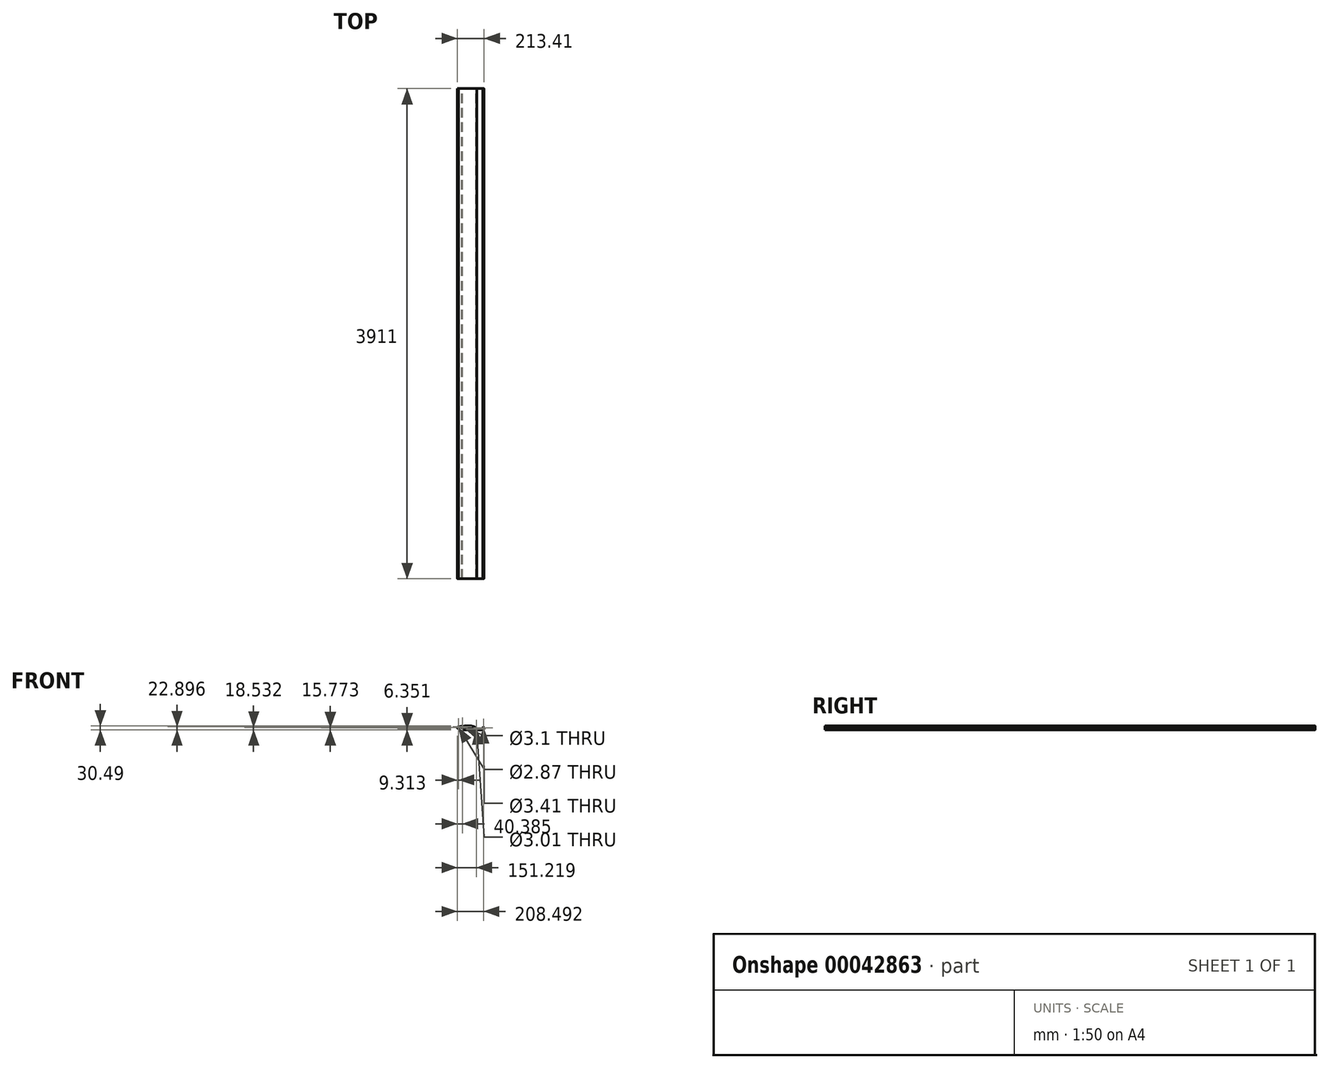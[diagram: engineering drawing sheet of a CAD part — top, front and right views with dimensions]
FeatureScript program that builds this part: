
annotation { "Feature Type Name" : "Feature", "Feature Type Description" : "" }
export const myFeature = defineFeature(function(context is Context, id is Id, definition is map)
    precondition{}
    {
        {
            var Q0;
            Q0=qCreatedBy(makeId("Front.planeOp"),FACE);
            var sketch = newSketch(context, id + "F0", { "sketchPlane" : qUnion([Q0])});
            skCircle(sketch, "E0", {"center": v(-106.3, 13.54) * mm, "radius": 1.44 * mm});
            skCircle(sketch, "E1", {"center": v(-75.23, 17.9) * mm, "radius": 1.55 * mm});
            skCircle(sketch, "E2", {"center": v(35.6, 1.36) * mm, "radius": 1.5 * mm});
            skCircle(sketch, "E3", {"center": v(92.88, 10.78) * mm, "radius": 1.7 * mm});
            skFitSpline(sketch, "E4", {"points": [v(-107.48, 19.59) * mm, v(-60.2, 23.95) * mm, v(-6.86, 24.97) * mm, v(22.27, 16.71) * mm, v(39.36, 3.6) * mm], "startDerivative": vector(161.35, 14.36) * mm, "endDerivative": vector(26.37, -21.19) * mm});
            skLineSegment(sketch, "E5", {"start": v(40.27, -1.32) * mm, "end": v(87.46, -1.24) * mm});
            skFitSpline(sketch, "E6", {"points": [v(40.3, -3.85) * mm, v(90, 0.2) * mm, v(93, 9.4) * mm], "startDerivative": vector(8.74, 2.96) * mm, "endDerivative": vector(0.7, 5.97) * mm});
            skLineSegment(sketch, "E7", {"start": v(92.97, 5.13) * mm, "end": v(86.47, 9.2) * mm});
            skLineSegment(sketch, "E8", {"start": v(86.47, 9.2) * mm, "end": v(91.56, 17) * mm});
            skLineSegment(sketch, "E9", {"start": v(96.31, 14.3) * mm, "end": v(91.56, 17) * mm});
            skLineSegment(sketch, "E10", {"start": v(-68.16, -4.99) * mm, "end": v(-80.63, 17.44) * mm});
            skLineSegment(sketch, "E11", {"start": v(-116.11, 7.62) * mm, "end": v(-113.4, 14.94) * mm});
            skLineSegment(sketch, "E12", {"start": v(-116.11, 7.62) * mm, "end": v(-111.23, 5.8) * mm});
            skLineSegment(sketch, "E13", {"start": v(-111.23, 5.8) * mm, "end": v(-109.3, 11.02) * mm});
            skArc(sketch, "E14", {"start": v(97.6, 9.4) * mm, "mid": v(97.64, 12.03) * mm, "end": v(96.31, 14.3) * mm});
            skArc(sketch, "E15", {"start": v(40.27, -1.32) * mm, "mid": v(40.61, 1.3) * mm, "end": v(39.35, 3.6) * mm});
            skArc(sketch, "E16", {"start": v(-107.48, 19.59) * mm, "mid": v(-111.19, 18.22) * mm, "end": v(-113.4, 14.94) * mm});
            skArc(sketch, "E17", {"start": v(-109.3, 11.02) * mm, "mid": v(-103.78, 10.54) * mm, "end": v(-103.3, 16.06) * mm});
            skLineSegment(sketch, "E18", {"start": v(-103.3, 16.06) * mm, "end": v(-80.63, 17.44) * mm});
            skLineSegment(sketch, "E19", {"start": v(-68.16, -4.99) * mm, "end": v(91.56, -4.99) * mm});
            skLineSegment(sketch, "E20", {"start": v(97.6, 9.4) * mm, "end": v(91.56, -4.99) * mm});
            skLineSegment(sketch, "E21", {"start": v(-72.14, 20.7) * mm, "end": v(-72.14, 13.78) * mm});
            skLineSegment(sketch, "E22", {"start": v(-72.14, 13.78) * mm, "end": v(-75.93, 13.78) * mm});
            skLineSegment(sketch, "E23", {"start": v(-75.93, 13.78) * mm, "end": v(-66.55, -2.48) * mm});
            skLineSegment(sketch, "E24", {"start": v(-66.55, -2.48) * mm, "end": v(31.06, -2.48) * mm});
            skLineSegment(sketch, "E25", {"start": v(31.06, -2.48) * mm, "end": v(31.06, 1.08) * mm});
            skLineSegment(sketch, "E26", {"start": v(31.06, 1.08) * mm, "end": v(33.93, 5.24) * mm});
            skFitSpline(sketch, "E27", {"points": [v(-107.28, 17.33) * mm, v(-103.91, 17.63) * mm, v(-97.2, 18.27) * mm, v(-87.04, 19.28) * mm, v(-78.4, 20.12) * mm, v(-71.32, 20.77) * mm, v(-65.91, 21.23) * mm, v(-60.39, 21.67) * mm, v(-54.72, 22.07) * mm, v(-48.96, 22.43) * mm, v(-41.23, 22.84) * mm, v(-33.5, 23.12) * mm, v(-25.98, 23.24) * mm, v(-20.49, 23.24) * mm, v(-15.2, 23.14) * mm, v(-10.15, 22.93) * mm, v(-5.41, 22.61) * mm, v(-1, 22.16) * mm, v(3.11, 21.54) * mm, v(8.3, 20.43) * mm, v(13.15, 18.86) * mm, v(17.9, 16.64) * mm, v(21.45, 14.62) * mm, v(25.08, 12.19) * mm, v(28.6, 9.57) * mm, v(31.84, 7) * mm, v(34.14, 5.07) * mm, v(35.66, 3.77) * mm, v(36.62, 2.94) * mm, v(37.4, 2.28) * mm, v(37.77, 1.96) * mm, v(37.94, 1.83) * mm]});
            skSolve(sketch);
        }
        {
            var Q0;
            Q0 = qSketchRegion(id + "F0", true);
            extrude(context, id + "F1", {"entities" : qUnion([Q0]), "depth" : 3911 * mm});
        }
        {
            var Q0;
            Q0=makeQuery(id+"F1.opExtrude","SWEPT_EDGE",EDGE,{"disambiguationData":[OSD([sQuery(id+"F0.wireOp",EDGE,"E11"),sQuery(id+"F0.wireOp",EDGE,"E12")])]});
            var Q1;
            Q1=makeQuery(id+"F1.opExtrude","SWEPT_EDGE",EDGE,{"disambiguationData":[OSD([sQuery(id+"F0.wireOp",EDGE,"E12"),sQuery(id+"F0.wireOp",EDGE,"E13")])]});
            var Q2;
            Q2=makeQuery(id+"F1.opExtrude","SWEPT_EDGE",EDGE,{"disambiguationData":[OSD([sQuery(id+"F0.wireOp",EDGE,"E10"),sQuery(id+"F0.wireOp",EDGE,"E19")])]});
            var Q3;
            Q3=makeQuery(id+"F1.opExtrude","SWEPT_EDGE",EDGE,{"disambiguationData":[OSD([sQuery(id+"F0.wireOp",EDGE,"E19"),sQuery(id+"F0.wireOp",EDGE,"E20")])]});
            var Q4;
            Q4=makeQuery(id+"F1.opExtrude","SWEPT_EDGE",EDGE,{"disambiguationData":[OSD([sQuery(id+"F0.wireOp",EDGE,"E21"),sQuery(id+"F0.wireOp",EDGE,"E22")])]});
            var Q5;
            Q5=makeQuery(id+"F1.opExtrude","SWEPT_EDGE",EDGE,{"disambiguationData":[OSD([sQuery(id+"F0.wireOp",EDGE,"E21"),sQuery(id+"F0.wireOp",EDGE,"E27")])]});
            var Q6;
            Q6=makeQuery(id+"F1.opExtrude","SWEPT_EDGE",EDGE,{"disambiguationData":[OSD([sQuery(id+"F0.wireOp",EDGE,"E26"),sQuery(id+"F0.wireOp",EDGE,"E27")])]});
            var Q7;
            Q7=makeQuery(id+"F1.opExtrude","SWEPT_EDGE",EDGE,{"disambiguationData":[OSD([sQuery(id+"F0.wireOp",EDGE,"E25"),sQuery(id+"F0.wireOp",EDGE,"E26")])]});
            var Q8;
            Q8=makeQuery(id+"F1.opExtrude","SWEPT_EDGE",EDGE,{"disambiguationData":[OSD([sQuery(id+"F0.wireOp",EDGE,"E24"),sQuery(id+"F0.wireOp",EDGE,"E25")])]});
            var Q9;
            Q9=makeQuery(id+"F1.opExtrude","SWEPT_EDGE",EDGE,{"disambiguationData":[OSD([sQuery(id+"F0.wireOp",EDGE,"E23"),sQuery(id+"F0.wireOp",EDGE,"E24")])]});
            var Q10;
            Q10=makeQuery(id+"F1.opExtrude","SWEPT_EDGE",EDGE,{"disambiguationData":[OSD([sQuery(id+"F0.wireOp",EDGE,"E8"),sQuery(id+"F0.wireOp",EDGE,"E9")])]});
            var Q11;
            Q11=makeQuery(id+"F1.opExtrude","SWEPT_EDGE",EDGE,{"disambiguationData":[OSD([sQuery(id+"F0.wireOp",EDGE,"E7"),sQuery(id+"F0.wireOp",EDGE,"E8")])]});
            var Q12;
            Q12=makeQuery(id+"F1.opExtrude","SWEPT_EDGE",EDGE,{"disambiguationData":[OSD([sQuery(id+"F0.wireOp",EDGE,"E6"),sQuery(id+"F0.wireOp",EDGE,"E7")])]});
            fillet(context, id + "F2", {"entities" : qUnion([Q0, Q1, Q2, Q3, Q4, Q5, Q6, Q7, Q8, Q9, Q10, Q11, Q12]), "radius" : 2 * mm, "tangentPropagation" : true, "rho" : 0.5, "crossSection" : FilletCrossSection.CONIC, "allowEdgeOverflow" : false});
        }
    });
